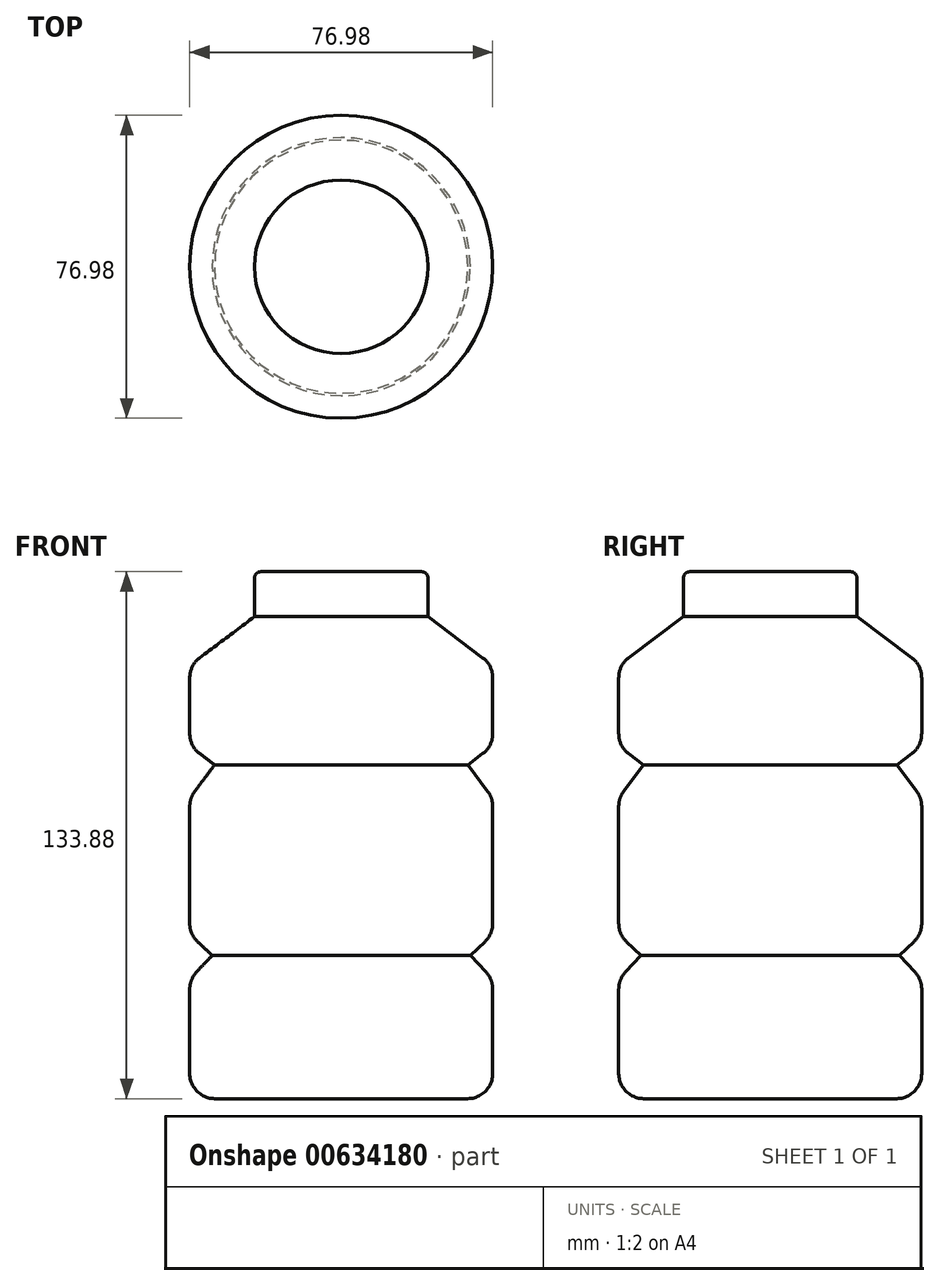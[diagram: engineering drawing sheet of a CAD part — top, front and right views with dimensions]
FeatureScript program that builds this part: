
annotation { "Feature Type Name" : "Feature", "Feature Type Description" : "" }
export const myFeature = defineFeature(function(context is Context, id is Id, definition is map)
    precondition{}
    {
        {
            var Q0;
            Q0=qCreatedBy(makeId("Front.planeOp"),FACE);
            var sketch = newSketch(context, id + "F0", { "sketchPlane" : qUnion([Q0])});
            skLineSegment(sketch, "E0", {"start": v(37.07, 0) * mm, "end": v(37.07, 26.12) * mm});
            skLineSegment(sketch, "E1", {"start": v(37.07, 26.12) * mm, "end": v(34.02, 32.23) * mm});
            skLineSegment(sketch, "E2", {"start": v(34.02, 32.23) * mm, "end": v(31.21, 39.11) * mm});
            skLineSegment(sketch, "E3", {"start": v(31.21, 39.11) * mm, "end": v(31.21, 43.44) * mm});
            skLineSegment(sketch, "E4", {"start": v(31.21, 43.44) * mm, "end": v(21.79, 43.44) * mm});
            skLineSegment(sketch, "E5", {"start": v(21.79, 43.44) * mm, "end": v(21.79, 39.11) * mm});
            skLineSegment(sketch, "E6", {"start": v(21.79, 39.11) * mm, "end": v(18.73, 32.23) * mm});
            skLineSegment(sketch, "E7", {"start": v(18.73, 32.23) * mm, "end": v(16.18, 26.12) * mm});
            skLineSegment(sketch, "E8", {"start": v(16.18, 26.12) * mm, "end": v(16.18, 0) * mm});
            skLineSegment(sketch, "E9", {"start": v(16.18, 0) * mm, "end": v(37.07, 0) * mm});
            skSolve(sketch);
        }
        {
            var Q0;
            Q0=qCreatedBy(makeId("Front.planeOp"),FACE);
            var sketch = newSketch(context, id + "F1", { "sketchPlane" : qUnion([Q0])});
            skCircle(sketch, "E10", {"center": v(78.26, 32.23) * mm, "radius": 22.5 * mm});
            skSolve(sketch);
        }
        {
            var Q0;
            Q0=makeQuery(id+"F0.imprint","IMPRINT",FACE,{"disambiguationData":[TD([[makeQuery(id+"F0.imprint","IMPRINT",EDGE,{"derivedFrom":sQuery(id+"F0.wireOp",EDGE,"E0")}),1.0]])]});
            extrude(context, id + "F2", {"entities" : qUnion([Q0]), "depth" : 12.7 * mm, "offsetDistance" : 25.4 * mm});
        }
        {
            var Q0;
            Q0=makeQuery(id+"F1.imprint","IMPRINT",FACE,{"disambiguationData":[TD([[makeQuery(id+"F1.imprint","IMPRINT",EDGE,{"derivedFrom":sQuery(id+"F1.wireOp",EDGE,"E10")}),1.0]])]});
            extrude(context, id + "F3", {"entities" : qUnion([Q0]), "depth" : 7.62 * mm, "offsetDistance" : 25.4 * mm});
        }
        {
            var Q0;
            Q0=qCreatedBy(makeId("Top.planeOp"),FACE);
            var sketch = newSketch(context, id + "F4", { "sketchPlane" : qUnion([Q0])});
            skLineSegment(sketch, "E11", {"start": v(0, 0) * mm, "end": v(-30.14, 0) * mm});
            skLineSegment(sketch, "E12", {"start": v(-30.14, 0) * mm, "end": v(-30.14, 17.96) * mm});
            skLineSegment(sketch, "E13", {"start": v(-30.14, 17.96) * mm, "end": v(0, 17.96) * mm});
            skLineSegment(sketch, "E14", {"start": v(0, 17.96) * mm, "end": v(0, 0) * mm});
            skSolve(sketch);
        }
        {
            var Q0;
            Q0 = qSketchRegion(id + "F4", true);
            extrude(context, id + "F5", {"entities" : qUnion([Q0]), "depth" : 2.54 * mm, "offsetDistance" : 25.4 * mm});
        }
        {
            var Q0;
            Q0=makeQuery(id+"F5.opExtrude","CAP_FACE",FACE,{"disambiguationData":[OSD([sQuery(id+"F4.wireOp",EDGE,"E11"),sQuery(id+"F4.wireOp",EDGE,"E12"),sQuery(id+"F4.wireOp",EDGE,"E13"),sQuery(id+"F4.wireOp",EDGE,"E14")])],"isStart":false});
            var sketch = newSketch(context, id + "F6", { "sketchPlane" : qUnion([Q0])});
            skLineSegment(sketch, "E15", {"start": v(-30.14, 2.42) * mm, "end": v(0, 2.42) * mm});
            skLineSegment(sketch, "E16", {"start": v(0, 2.42) * mm, "end": v(2.98, 2.42) * mm});
            skLineSegment(sketch, "E17", {"start": v(2.98, 2.42) * mm, "end": v(5.02, 4.46) * mm});
            skLineSegment(sketch, "E18", {"start": v(5.02, 4.46) * mm, "end": v(5.02, 7.26) * mm});
            skLineSegment(sketch, "E19", {"start": v(5.02, 7.26) * mm, "end": v(2.98, 7.26) * mm});
            skLineSegment(sketch, "E20", {"start": v(2.98, 7.26) * mm, "end": v(0, 7.26) * mm});
            skLineSegment(sketch, "E21", {"start": v(0, 7.26) * mm, "end": v(-30.14, 7.26) * mm});
            skLineSegment(sketch, "E22", {"start": v(-30.14, 7.26) * mm, "end": v(-32.7, 7.26) * mm});
            skLineSegment(sketch, "E23", {"start": v(-35.75, 7.26) * mm, "end": v(-35.75, 4.46) * mm});
            skLineSegment(sketch, "E24", {"start": v(-35.75, 4.46) * mm, "end": v(-30.14, 2.42) * mm});
            skLineSegment(sketch, "E25", {"start": v(-35.75, 7.26) * mm, "end": v(-30.14, 7.26) * mm});
            skLineSegment(sketch, "E26", {"start": v(0, 11.85) * mm, "end": v(-30.14, 11.85) * mm});
            skLineSegment(sketch, "E27", {"start": v(-30.14, 11.85) * mm, "end": v(-32.7, 11.85) * mm});
            skLineSegment(sketch, "E28", {"start": v(-32.7, 11.85) * mm, "end": v(-32.7, 14.4) * mm});
            skLineSegment(sketch, "E29", {"start": v(-32.7, 14.4) * mm, "end": v(-30.14, 14.4) * mm});
            skLineSegment(sketch, "E30", {"start": v(-30.14, 14.4) * mm, "end": v(0, 14.4) * mm});
            skLineSegment(sketch, "E31", {"start": v(0, 14.4) * mm, "end": v(5.02, 14.4) * mm});
            skLineSegment(sketch, "E32", {"start": v(5.02, 14.4) * mm, "end": v(2.98, 11.85) * mm});
            skLineSegment(sketch, "E33", {"start": v(2.98, 11.85) * mm, "end": v(0, 11.85) * mm});
            skSolve(sketch);
        }
        {
            var Q0;
            Q0 = qSketchRegion(id + "F6", true);
            extrude(context, id + "F7", {"entities" : qUnion([Q0]), "operationType" : NewBodyOperationType.ADD, "depth" : 1.27 * mm, "offsetDistance" : 25.4 * mm});
        }
        {
            var Q0;
            Q0=makeQuery(id+"F3.opExtrude","SWEPT_BODY",BODY,{"disambiguationData":[OSD([sQuery(id+"F1.wireOp",EDGE,"E10")])]});
            deleteBodies(context, id + "F8", {"entities" : qUnion([Q0])});
        }
        {
            var Q0;
            Q0=makeQuery(id+"F5.opExtrude","SWEPT_BODY",BODY,{"disambiguationData":[OSD([sQuery(id+"F4.wireOp",EDGE,"E11"),sQuery(id+"F4.wireOp",EDGE,"E12"),sQuery(id+"F4.wireOp",EDGE,"E13"),sQuery(id+"F4.wireOp",EDGE,"E14")])]});
            deleteBodies(context, id + "F9", {"entities" : qUnion([Q0])});
        }
        {
            var Q0;
            Q0=makeQuery(id+"F2.opExtrude","SWEPT_BODY",BODY,{"disambiguationData":[OSD([sQuery(id+"F0.wireOp",EDGE,"E0"),sQuery(id+"F0.wireOp",EDGE,"E1"),sQuery(id+"F0.wireOp",EDGE,"E2"),sQuery(id+"F0.wireOp",EDGE,"E3"),sQuery(id+"F0.wireOp",EDGE,"E4"),sQuery(id+"F0.wireOp",EDGE,"E5"),sQuery(id+"F0.wireOp",EDGE,"E6"),sQuery(id+"F0.wireOp",EDGE,"E7"),sQuery(id+"F0.wireOp",EDGE,"E8"),sQuery(id+"F0.wireOp",EDGE,"E9")])]});
            deleteBodies(context, id + "F10", {"entities" : qUnion([Q0])});
        }
        {
            var Q0;
            Q0=qCreatedBy(makeId("Front.planeOp"),FACE);
            var sketch = newSketch(context, id + "F11", { "sketchPlane" : qUnion([Q0])});
            skLineSegment(sketch, "E34", {"start": v(0, 67.41) * mm, "end": v(-20.45, 67.41) * mm});
            skLineSegment(sketch, "E35", {"start": v(-22.03, 65.82) * mm, "end": v(-22.03, 56) * mm});
            skLineSegment(sketch, "E36", {"start": v(-22.03, 56) * mm, "end": v(-35.95, 45.56) * mm});
            skLineSegment(sketch, "E37", {"start": v(-38.49, 40.48) * mm, "end": v(-38.49, 26.26) * mm});
            skLineSegment(sketch, "E38", {"start": v(-35.95, 21.18) * mm, "end": v(-32.16, 18.34) * mm});
            skLineSegment(sketch, "E39", {"start": v(-32.16, 18.34) * mm, "end": v(-37.22, 11.6) * mm});
            skLineSegment(sketch, "E40", {"start": v(-38.49, 7.78) * mm, "end": v(-38.49, -21.96) * mm});
            skLineSegment(sketch, "E41", {"start": v(-36.5, -26.58) * mm, "end": v(-32.8, -30.08) * mm});
            skLineSegment(sketch, "E42", {"start": v(-32.8, -30.08) * mm, "end": v(-36.75, -34.27) * mm});
            skLineSegment(sketch, "E43", {"start": v(-38.49, -38.63) * mm, "end": v(-38.49, -60.12) * mm});
            skLineSegment(sketch, "E44", {"start": v(-32.14, -66.47) * mm, "end": v(0, -66.47) * mm});
            skLineSegment(sketch, "E45", {"start": v(0, -66.47) * mm, "end": v(0, 67.41) * mm});
            skPoint(sketch, "E46.visualSharp", {"position": v(-38.49, 43.65) * mm});
            skArc(sketch, "E46.filletArc", {"start": v(-35.95, 45.56) * mm, "mid": v(-37.82, 43.32) * mm, "end": v(-38.49, 40.48) * mm});
            skPoint(sketch, "E47.visualSharp", {"position": v(-38.49, 23.08) * mm});
            skArc(sketch, "E47.filletArc", {"start": v(-38.49, 26.26) * mm, "mid": v(-37.82, 23.42) * mm, "end": v(-35.95, 21.18) * mm});
            skPoint(sketch, "E48.visualSharp", {"position": v(-38.49, 9.9) * mm});
            skArc(sketch, "E48.filletArc", {"start": v(-37.22, 11.6) * mm, "mid": v(-38.16, 9.79) * mm, "end": v(-38.49, 7.78) * mm});
            skPoint(sketch, "E49.visualSharp", {"position": v(-38.49, -24.7) * mm});
            skArc(sketch, "E49.filletArc", {"start": v(-38.49, -21.96) * mm, "mid": v(-37.97, -24.48) * mm, "end": v(-36.5, -26.58) * mm});
            skPoint(sketch, "E50.visualSharp", {"position": v(-38.49, -36.1) * mm});
            skArc(sketch, "E50.filletArc", {"start": v(-36.75, -34.27) * mm, "mid": v(-38.04, -36.29) * mm, "end": v(-38.49, -38.63) * mm});
            skPoint(sketch, "E51.visualSharp", {"position": v(-38.49, -66.47) * mm});
            skArc(sketch, "E51.filletArc", {"start": v(-38.49, -60.12) * mm, "mid": v(-36.63, -64.6) * mm, "end": v(-32.14, -66.47) * mm});
            skPoint(sketch, "E52.visualSharp", {"position": v(-22.03, 67.41) * mm});
            skArc(sketch, "E52.filletArc", {"start": v(-20.45, 67.41) * mm, "mid": v(-21.57, 66.95) * mm, "end": v(-22.03, 65.82) * mm});
            skLineSegment(sketch, "E53", {"start": v(-22.03, 56) * mm, "end": v(0, 56) * mm});
            skSolve(sketch);
        }
        {
            var Q0;
            Q0=makeQuery(id+"F11.imprint","IMPRINT",FACE,{"disambiguationData":[TD([[makeQuery(id+"F11.imprint","IMPRINT",EDGE,{"derivedFrom":sQuery(id+"F11.wireOp",EDGE,"E36")}),1.0]])]});
            var Q1;
            {var subQ1=sQuery(id+"F11.wireOp",EDGE,"E34");Q1=makeQuery(id+"F11.imprint","IMPRINT",FACE,{"disambiguationData":[TD([[makeQuery(id+"F11.imprint","IMPRINT",EDGE,{"derivedFrom":subQ1}),1.0]])]});}
            var Q2;
            Q2=sQuery(id+"F11.wireOp",EDGE,"E45");
            revolve(context, id + "F12", {"entities" : qUnion([Q0, Q1]), "axis" : qUnion([Q2]), "revolveType" : RevolveType.FULL});
        }
    });
